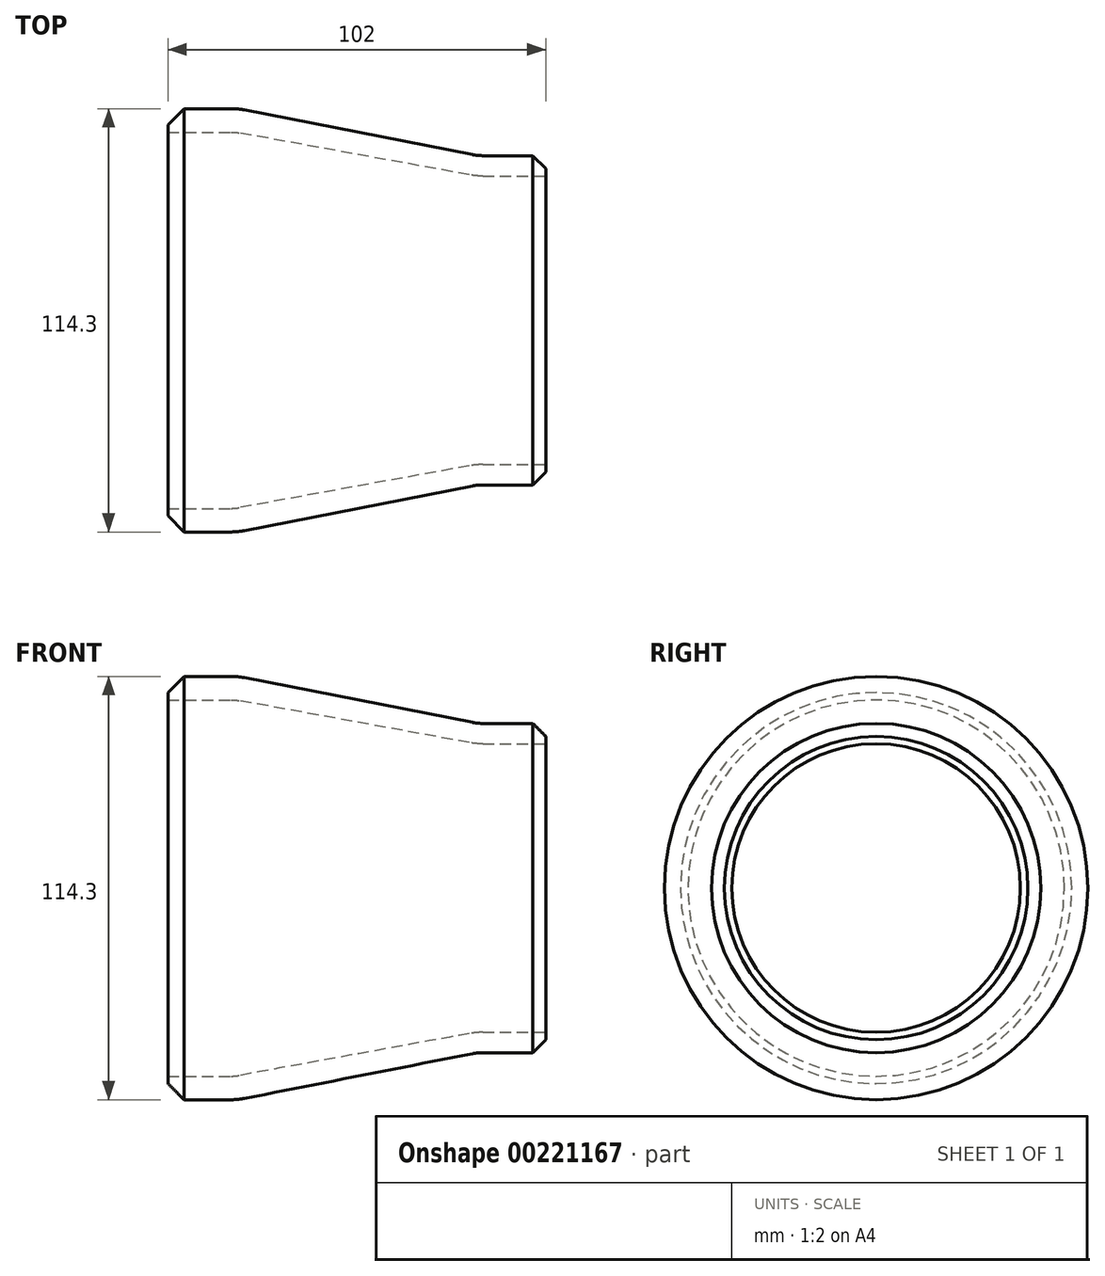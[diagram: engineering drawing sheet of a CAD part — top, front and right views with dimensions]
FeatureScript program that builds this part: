
annotation { "Feature Type Name" : "Feature", "Feature Type Description" : "" }
export const myFeature = defineFeature(function(context is Context, id is Id, definition is map)
    precondition{}
    {
        {
            assignVariable(context, id + "F0", {"name" : "T", "anyValue" : 6.35});
        }
        {
            assignVariable(context, id + "F1", {"name" : "t", "anyValue" : 5.5});
        }
        {
            var Q0;
            Q0=qCreatedBy(makeId("Front.planeOp"),FACE);
            var sketch = newSketch(context, id + "F2", { "sketchPlane" : qUnion([Q0])});
            skLineSegment(sketch, "E0", {"start": v(0, 50.8) * mm, "end": v(0, 57.15) * mm});
            skLineSegment(sketch, "E1", {"start": v(0, 57.15) * mm, "end": v(17, 57.15) * mm});
            skLineSegment(sketch, "E2", {"start": v(20.67, 56.8) * mm, "end": v(82.15, 44.73) * mm});
            skLineSegment(sketch, "E3", {"start": v(85, 44.45) * mm, "end": v(102, 44.45) * mm});
            skLineSegment(sketch, "E4", {"start": v(102, 44.45) * mm, "end": v(102, 38.95) * mm});
            skLineSegment(sketch, "E5", {"start": v(102, 0) * mm, "end": v(0, 0) * mm, "construction": true});
            skLineSegment(sketch, "E6", {"start": v(0, 50.8) * mm, "end": v(17, 50.8) * mm});
            skLineSegment(sketch, "E7", {"start": v(19.28, 50.6) * mm, "end": v(81.36, 39.28) * mm});
            skLineSegment(sketch, "E8", {"start": v(85, 38.95) * mm, "end": v(102, 38.95) * mm});
            skPoint(sketch, "E9.visualSharp", {"position": v(18.85, 57.15) * mm});
            skArc(sketch, "E9.filletArc", {"start": v(20.67, 56.8) * mm, "mid": v(18.84, 57.06) * mm, "end": v(17, 57.15) * mm});
            skPoint(sketch, "E10.visualSharp", {"position": v(18.15, 50.8) * mm});
            skArc(sketch, "E10.filletArc", {"start": v(19.28, 50.6) * mm, "mid": v(18.14, 50.75) * mm, "end": v(17, 50.8) * mm});
            skPoint(sketch, "E11.visualSharp", {"position": v(83.56, 44.45) * mm});
            skArc(sketch, "E11.filletArc", {"start": v(82.15, 44.73) * mm, "mid": v(83.57, 44.52) * mm, "end": v(85, 44.45) * mm});
            skPoint(sketch, "E12.visualSharp", {"position": v(83.16, 38.95) * mm});
            skArc(sketch, "E12.filletArc", {"start": v(81.36, 39.28) * mm, "mid": v(83.17, 39.03) * mm, "end": v(85, 38.95) * mm});
            skSolve(sketch);
        }
        {
            var Q0;
            Q0=makeQuery(id+"F2.imprint","IMPRINT",FACE,{"disambiguationData":[TD([[makeQuery(id+"F2.imprint","IMPRINT",EDGE,{"derivedFrom":sQuery(id+"F2.wireOp",EDGE,"E0")}),-1.0]])]});
            var Q1;
            Q1=sQuery(id+"F2.wireOp",EDGE,"E5");
            revolve(context, id + "F3", {"entities" : qUnion([Q0]), "axis" : qUnion([Q1]), "revolveType" : RevolveType.FULL});
        }
        {
            var Q0;
            Q0=makeQuery(id+"F3.opRevolve","SWEPT_EDGE",EDGE,{"disambiguationData":[OSD([sQuery(id+"F2.wireOp",EDGE,"E3"),sQuery(id+"F2.wireOp",EDGE,"E4")])]});
            chamfer(context, id + "F4", {"entities" : qUnion([Q0]), "width" : (getVariable(context, 't') - 2) * mm, "tangentPropagation" : true});
        }
        {
            var Q0;
            Q0=makeQuery(id+"F3.opRevolve","SWEPT_EDGE",EDGE,{"disambiguationData":[OSD([sQuery(id+"F2.wireOp",EDGE,"E0"),sQuery(id+"F2.wireOp",EDGE,"E1")])]});
            chamfer(context, id + "F5", {"entities" : qUnion([Q0]), "width" : (getVariable(context, 'T') - 2) * mm, "tangentPropagation" : true});
        }
    });
